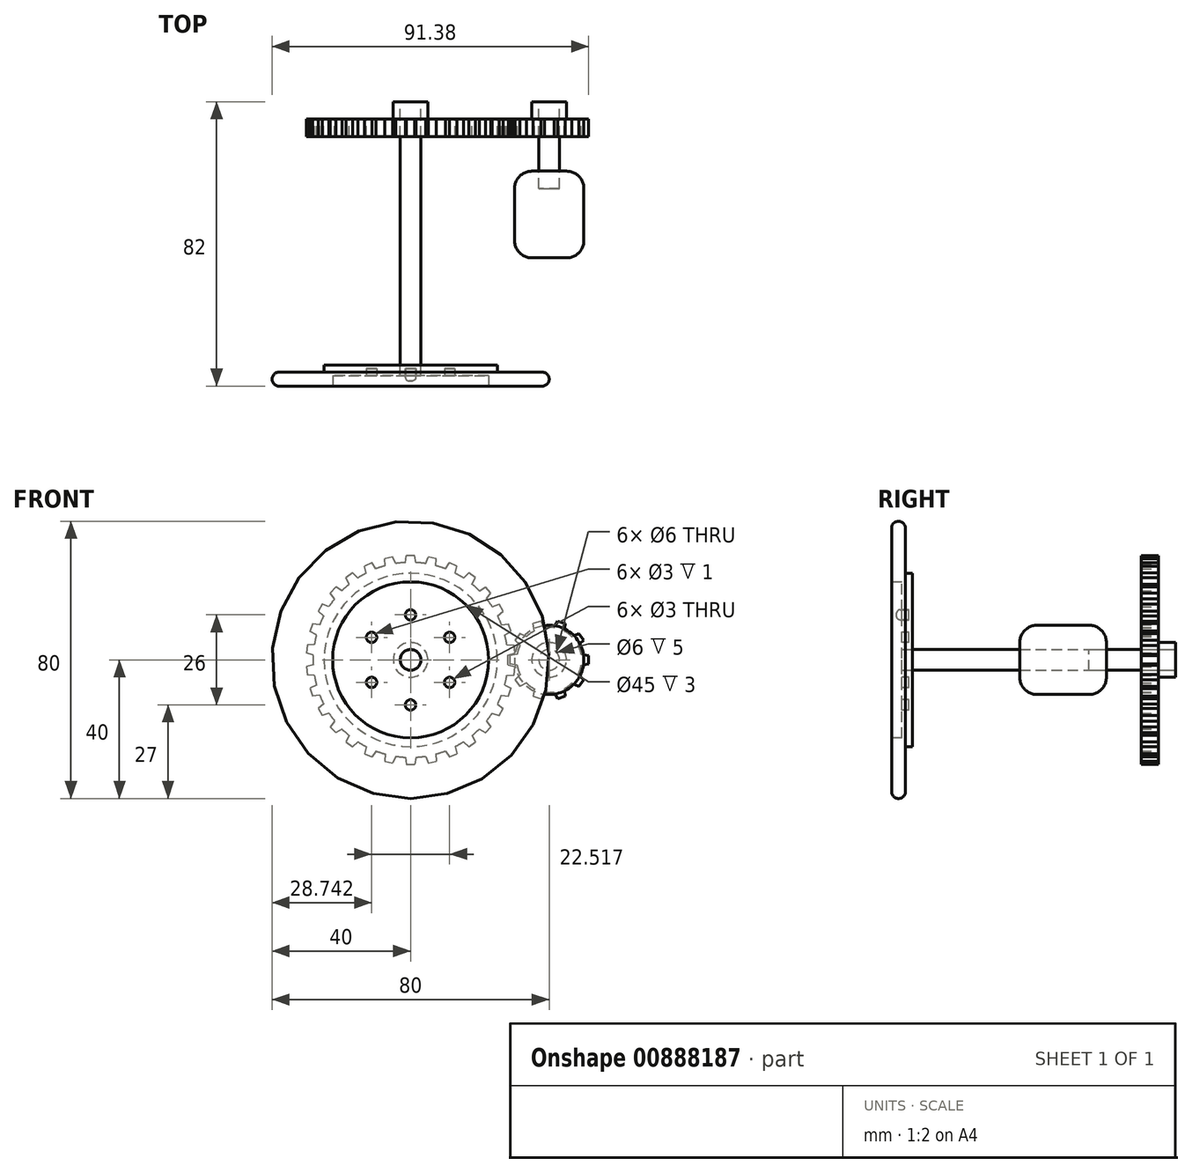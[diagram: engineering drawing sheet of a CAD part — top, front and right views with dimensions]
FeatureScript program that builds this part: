
annotation { "Feature Type Name" : "Feature", "Feature Type Description" : "" }
export const myFeature = defineFeature(function(context is Context, id is Id, definition is map)
    precondition{}
    {
        {
            var Q0;
            Q0=qCreatedBy(makeId("Front.planeOp"),FACE);
            var sketch = newSketch(context, id + "F0", { "sketchPlane" : qUnion([Q0])});
            skCircle(sketch, "E0", {"center": v(0, 0) * mm, "radius": 5 * mm});
            skCircle(sketch, "E1", {"center": v(0, 0) * mm, "radius": 3 * mm});
            skCircle(sketch, "E2", {"center": v(40, 0) * mm, "radius": 5 * mm});
            skCircle(sketch, "E3", {"center": v(40, 0) * mm, "radius": 3 * mm});
            skSolve(sketch);
        }
        {
            var Q0;
            Q0=makeQuery(id+"F0.imprint","IMPRINT",FACE,{"disambiguationData":[TD([[makeQuery(id+"F0.imprint","IMPRINT",EDGE,{"derivedFrom":sQuery(id+"F0.wireOp",EDGE,"E1")}),1.0]])]});
            extrude(context, id + "F1", {"entities" : qUnion([Q0]), "depth" : 80 * mm, "offsetDistance" : 25 * mm});
        }
        {
            var Q0;
            Q0=makeQuery(id+"F0.imprint","IMPRINT",FACE,{"disambiguationData":[TD([[makeQuery(id+"F0.imprint","IMPRINT",EDGE,{"derivedFrom":sQuery(id+"F0.wireOp",EDGE,"E0")}),1.0]])]});
            extrude(context, id + "F2", {"entities" : qUnion([Q0]), "depth" : 5 * mm, "offsetDistance" : 25 * mm});
        }
        {
            var Q0;
            Q0=makeQuery(id+"F0.imprint","IMPRINT",FACE,{"disambiguationData":[TD([[makeQuery(id+"F0.imprint","IMPRINT",EDGE,{"derivedFrom":sQuery(id+"F0.wireOp",EDGE,"E2")}),1.0]])]});
            extrude(context, id + "F3", {"entities" : qUnion([Q0]), "depth" : 5 * mm, "offsetDistance" : 25 * mm});
        }
        {
            var Q0;
            Q0=makeQuery(id+"F0.imprint","IMPRINT",FACE,{"disambiguationData":[TD([[makeQuery(id+"F0.imprint","IMPRINT",EDGE,{"derivedFrom":sQuery(id+"F0.wireOp",EDGE,"E3")}),1.0]])]});
            extrude(context, id + "F4", {"entities" : qUnion([Q0]), "depth" : 25 * mm, "offsetDistance" : 25 * mm});
        }
        {
            var Q0;
            Q0=makeQuery(id+"F2.opExtrude","CAP_FACE",FACE,{"disambiguationData":[OSD([sQuery(id+"F0.wireOp",EDGE,"E0"),sQuery(id+"F0.wireOp",EDGE,"E1")])],"isStart":false});
            var sketch = newSketch(context, id + "F5", { "sketchPlane" : qUnion([Q0])});
            skCircle(sketch, "E4", {"center": v(0, 0) * mm, "radius": 28.12 * mm});
            skLineSegment(sketch, "E5", {"start": v(1.54, 28.08) * mm, "end": v(1.18, 30.12) * mm});
            skLineSegment(sketch, "E6", {"start": v(1.18, 30.12) * mm, "end": v(0, 30.12) * mm});
            skLineSegment(sketch, "E7.MirrorCS", {"start": v(-1.18, 30.13) * mm, "end": v(0, 30.13) * mm});
            skLineSegment(sketch, "E8.MirrorCS", {"start": v(-1.54, 28.08) * mm, "end": v(-1.18, 30.12) * mm});
            skLineSegment(sketch, "E9.1.0", {"start": v(-4.33, 27.79) * mm, "end": v(-5.11, 29.71) * mm});
            skLineSegment(sketch, "E9.1.1", {"start": v(-5.11, 29.71) * mm, "end": v(-6.26, 29.47) * mm});
            skLineSegment(sketch, "E9.1.2", {"start": v(-7.42, 29.22) * mm, "end": v(-6.26, 29.47) * mm});
            skLineSegment(sketch, "E9.1.3", {"start": v(-7.34, 27.15) * mm, "end": v(-7.42, 29.22) * mm});
            skLineSegment(sketch, "E9.2.0", {"start": v(-10.02, 26.28) * mm, "end": v(-11.18, 28) * mm});
            skLineSegment(sketch, "E9.2.1", {"start": v(-11.18, 28) * mm, "end": v(-12.25, 27.52) * mm});
            skLineSegment(sketch, "E9.2.2", {"start": v(-13.33, 27.04) * mm, "end": v(-12.25, 27.52) * mm});
            skLineSegment(sketch, "E9.2.3", {"start": v(-12.83, 25.03) * mm, "end": v(-13.33, 27.04) * mm});
            skLineSegment(sketch, "E10.1.3.0", {"start": v(-15.26, 23.62) * mm, "end": v(-16.75, 25.06) * mm});
            skLineSegment(sketch, "E10.3.3.0", {"start": v(-16.75, 25.06) * mm, "end": v(-17.7, 24.37) * mm});
            skLineSegment(sketch, "E10.6.3.0", {"start": v(-18.66, 23.68) * mm, "end": v(-17.7, 24.37) * mm});
            skLineSegment(sketch, "E10.9.3.0", {"start": v(-17.75, 21.82) * mm, "end": v(-18.66, 23.68) * mm});
            skLineSegment(sketch, "E10.1.4.0", {"start": v(-19.84, 19.93) * mm, "end": v(-21.6, 21.03) * mm});
            skLineSegment(sketch, "E10.3.4.0", {"start": v(-21.6, 21.03) * mm, "end": v(-22.39, 20.16) * mm});
            skLineSegment(sketch, "E10.6.4.0", {"start": v(-23.18, 19.28) * mm, "end": v(-22.39, 20.16) * mm});
            skLineSegment(sketch, "E10.9.4.0", {"start": v(-21.9, 17.65) * mm, "end": v(-23.18, 19.28) * mm});
            skLineSegment(sketch, "E10.1.5.0", {"start": v(-23.55, 15.37) * mm, "end": v(-25.5, 16.08) * mm});
            skLineSegment(sketch, "E10.3.5.0", {"start": v(-25.5, 16.08) * mm, "end": v(-26.09, 15.06) * mm});
            skLineSegment(sketch, "E10.6.5.0", {"start": v(-26.68, 14.04) * mm, "end": v(-26.09, 15.06) * mm});
            skLineSegment(sketch, "E10.9.5.0", {"start": v(-25.09, 12.7) * mm, "end": v(-26.68, 14.04) * mm});
            skLineSegment(sketch, "E10.1.6.0", {"start": v(-26.23, 10.14) * mm, "end": v(-28.29, 10.43) * mm});
            skLineSegment(sketch, "E10.3.6.0", {"start": v(-28.29, 10.43) * mm, "end": v(-28.65, 9.3) * mm});
            skLineSegment(sketch, "E10.6.6.0", {"start": v(-29.01, 8.19) * mm, "end": v(-28.65, 9.3) * mm});
            skLineSegment(sketch, "E10.9.6.0", {"start": v(-27.18, 7.22) * mm, "end": v(-29.01, 8.19) * mm});
            skLineSegment(sketch, "E10.1.7.0", {"start": v(-27.77, 4.47) * mm, "end": v(-29.84, 4.32) * mm});
            skLineSegment(sketch, "E10.3.7.0", {"start": v(-29.84, 4.32) * mm, "end": v(-29.96, 3.15) * mm});
            skLineSegment(sketch, "E10.6.7.0", {"start": v(-30.08, 1.98) * mm, "end": v(-29.96, 3.15) * mm});
            skLineSegment(sketch, "E10.9.7.0", {"start": v(-28.09, 1.4) * mm, "end": v(-30.08, 1.98) * mm});
            skLineSegment(sketch, "E10.1.8.0", {"start": v(-28.09, -1.4) * mm, "end": v(-30.08, -1.98) * mm});
            skLineSegment(sketch, "E10.3.8.0", {"start": v(-30.08, -1.98) * mm, "end": v(-29.96, -3.15) * mm});
            skLineSegment(sketch, "E10.6.8.0", {"start": v(-29.84, -4.32) * mm, "end": v(-29.96, -3.15) * mm});
            skLineSegment(sketch, "E10.9.8.0", {"start": v(-27.77, -4.47) * mm, "end": v(-29.84, -4.32) * mm});
            skLineSegment(sketch, "E10.1.9.0", {"start": v(-27.18, -7.22) * mm, "end": v(-29.01, -8.19) * mm});
            skLineSegment(sketch, "E10.3.9.0", {"start": v(-29.01, -8.19) * mm, "end": v(-28.65, -9.3) * mm});
            skLineSegment(sketch, "E10.6.9.0", {"start": v(-28.29, -10.43) * mm, "end": v(-28.65, -9.3) * mm});
            skLineSegment(sketch, "E10.9.9.0", {"start": v(-26.23, -10.14) * mm, "end": v(-28.29, -10.43) * mm});
            skLineSegment(sketch, "E10.1.10.0", {"start": v(-25.09, -12.7) * mm, "end": v(-26.68, -14.04) * mm});
            skLineSegment(sketch, "E10.3.10.0", {"start": v(-26.68, -14.04) * mm, "end": v(-26.09, -15.06) * mm});
            skLineSegment(sketch, "E10.6.10.0", {"start": v(-25.5, -16.08) * mm, "end": v(-26.09, -15.06) * mm});
            skLineSegment(sketch, "E10.9.10.0", {"start": v(-23.55, -15.37) * mm, "end": v(-25.5, -16.08) * mm});
            skLineSegment(sketch, "E10.1.11.0", {"start": v(-21.9, -17.65) * mm, "end": v(-23.18, -19.28) * mm});
            skLineSegment(sketch, "E10.3.11.0", {"start": v(-23.18, -19.28) * mm, "end": v(-22.39, -20.16) * mm});
            skLineSegment(sketch, "E10.6.11.0", {"start": v(-21.6, -21.03) * mm, "end": v(-22.39, -20.16) * mm});
            skLineSegment(sketch, "E10.9.11.0", {"start": v(-19.84, -19.93) * mm, "end": v(-21.6, -21.03) * mm});
            skLineSegment(sketch, "E10.1.12.0", {"start": v(-17.75, -21.82) * mm, "end": v(-18.66, -23.68) * mm});
            skLineSegment(sketch, "E10.3.12.0", {"start": v(-18.66, -23.68) * mm, "end": v(-17.7, -24.37) * mm});
            skLineSegment(sketch, "E10.6.12.0", {"start": v(-16.75, -25.06) * mm, "end": v(-17.7, -24.37) * mm});
            skLineSegment(sketch, "E10.9.12.0", {"start": v(-15.26, -23.62) * mm, "end": v(-16.75, -25.06) * mm});
            skLineSegment(sketch, "E10.1.13.0", {"start": v(-12.83, -25.03) * mm, "end": v(-13.33, -27.04) * mm});
            skLineSegment(sketch, "E10.3.13.0", {"start": v(-13.33, -27.04) * mm, "end": v(-12.25, -27.52) * mm});
            skLineSegment(sketch, "E10.6.13.0", {"start": v(-11.18, -28) * mm, "end": v(-12.25, -27.52) * mm});
            skLineSegment(sketch, "E10.9.13.0", {"start": v(-10.02, -26.28) * mm, "end": v(-11.18, -28) * mm});
            skLineSegment(sketch, "E10.1.14.0", {"start": v(-7.34, -27.15) * mm, "end": v(-7.42, -29.22) * mm});
            skLineSegment(sketch, "E10.3.14.0", {"start": v(-7.42, -29.22) * mm, "end": v(-6.26, -29.47) * mm});
            skLineSegment(sketch, "E10.6.14.0", {"start": v(-5.11, -29.71) * mm, "end": v(-6.26, -29.47) * mm});
            skLineSegment(sketch, "E10.9.14.0", {"start": v(-4.33, -27.79) * mm, "end": v(-5.11, -29.71) * mm});
            skLineSegment(sketch, "E10.1.15.0", {"start": v(-1.54, -28.08) * mm, "end": v(-1.18, -30.12) * mm});
            skLineSegment(sketch, "E10.3.15.0", {"start": v(-1.18, -30.13) * mm, "end": v(0, -30.13) * mm});
            skLineSegment(sketch, "E10.6.15.0", {"start": v(1.18, -30.13) * mm, "end": v(0, -30.13) * mm});
            skLineSegment(sketch, "E10.9.15.0", {"start": v(1.54, -28.08) * mm, "end": v(1.18, -30.12) * mm});
            skLineSegment(sketch, "E10.1.16.0", {"start": v(4.33, -27.79) * mm, "end": v(5.11, -29.71) * mm});
            skLineSegment(sketch, "E10.3.16.0", {"start": v(5.11, -29.71) * mm, "end": v(6.26, -29.47) * mm});
            skLineSegment(sketch, "E10.6.16.0", {"start": v(7.42, -29.22) * mm, "end": v(6.26, -29.47) * mm});
            skLineSegment(sketch, "E10.9.16.0", {"start": v(7.34, -27.15) * mm, "end": v(7.42, -29.22) * mm});
            skLineSegment(sketch, "E10.1.17.0", {"start": v(10.02, -26.28) * mm, "end": v(11.18, -28) * mm});
            skLineSegment(sketch, "E10.3.17.0", {"start": v(11.18, -28) * mm, "end": v(12.25, -27.52) * mm});
            skLineSegment(sketch, "E10.6.17.0", {"start": v(13.33, -27.04) * mm, "end": v(12.25, -27.52) * mm});
            skLineSegment(sketch, "E10.9.17.0", {"start": v(12.83, -25.03) * mm, "end": v(13.33, -27.04) * mm});
            skLineSegment(sketch, "E10.1.18.0", {"start": v(15.26, -23.62) * mm, "end": v(16.75, -25.06) * mm});
            skLineSegment(sketch, "E10.3.18.0", {"start": v(16.75, -25.06) * mm, "end": v(17.7, -24.37) * mm});
            skLineSegment(sketch, "E10.6.18.0", {"start": v(18.66, -23.68) * mm, "end": v(17.7, -24.37) * mm});
            skLineSegment(sketch, "E10.9.18.0", {"start": v(17.75, -21.82) * mm, "end": v(18.66, -23.68) * mm});
            skLineSegment(sketch, "E10.1.19.0", {"start": v(19.84, -19.93) * mm, "end": v(21.6, -21.03) * mm});
            skLineSegment(sketch, "E10.3.19.0", {"start": v(21.6, -21.03) * mm, "end": v(22.39, -20.16) * mm});
            skLineSegment(sketch, "E10.6.19.0", {"start": v(23.18, -19.28) * mm, "end": v(22.39, -20.16) * mm});
            skLineSegment(sketch, "E10.9.19.0", {"start": v(21.9, -17.65) * mm, "end": v(23.18, -19.28) * mm});
            skLineSegment(sketch, "E10.1.20.0", {"start": v(23.55, -15.37) * mm, "end": v(25.5, -16.08) * mm});
            skLineSegment(sketch, "E10.3.20.0", {"start": v(25.5, -16.08) * mm, "end": v(26.09, -15.06) * mm});
            skLineSegment(sketch, "E10.6.20.0", {"start": v(26.68, -14.04) * mm, "end": v(26.09, -15.06) * mm});
            skLineSegment(sketch, "E10.9.20.0", {"start": v(25.09, -12.7) * mm, "end": v(26.68, -14.04) * mm});
            skLineSegment(sketch, "E10.1.21.0", {"start": v(26.23, -10.14) * mm, "end": v(28.29, -10.43) * mm});
            skLineSegment(sketch, "E10.3.21.0", {"start": v(28.29, -10.43) * mm, "end": v(28.65, -9.3) * mm});
            skLineSegment(sketch, "E10.6.21.0", {"start": v(29.01, -8.19) * mm, "end": v(28.65, -9.3) * mm});
            skLineSegment(sketch, "E10.9.21.0", {"start": v(27.18, -7.22) * mm, "end": v(29.01, -8.19) * mm});
            skLineSegment(sketch, "E10.1.22.0", {"start": v(27.77, -4.47) * mm, "end": v(29.84, -4.32) * mm});
            skLineSegment(sketch, "E10.3.22.0", {"start": v(29.84, -4.32) * mm, "end": v(29.96, -3.15) * mm});
            skLineSegment(sketch, "E10.6.22.0", {"start": v(30.08, -1.98) * mm, "end": v(29.96, -3.15) * mm});
            skLineSegment(sketch, "E10.9.22.0", {"start": v(28.09, -1.4) * mm, "end": v(30.08, -1.98) * mm});
            skLineSegment(sketch, "E10.1.23.0", {"start": v(28.09, 1.4) * mm, "end": v(30.08, 1.98) * mm});
            skLineSegment(sketch, "E10.3.23.0", {"start": v(30.08, 1.98) * mm, "end": v(29.96, 3.15) * mm});
            skLineSegment(sketch, "E10.6.23.0", {"start": v(29.84, 4.32) * mm, "end": v(29.96, 3.15) * mm});
            skLineSegment(sketch, "E10.9.23.0", {"start": v(27.77, 4.47) * mm, "end": v(29.84, 4.32) * mm});
            skLineSegment(sketch, "E10.1.24.0", {"start": v(27.18, 7.22) * mm, "end": v(29.01, 8.19) * mm});
            skLineSegment(sketch, "E10.3.24.0", {"start": v(29.01, 8.19) * mm, "end": v(28.65, 9.3) * mm});
            skLineSegment(sketch, "E10.6.24.0", {"start": v(28.29, 10.43) * mm, "end": v(28.65, 9.3) * mm});
            skLineSegment(sketch, "E10.9.24.0", {"start": v(26.23, 10.14) * mm, "end": v(28.29, 10.43) * mm});
            skLineSegment(sketch, "E10.1.25.0", {"start": v(25.09, 12.7) * mm, "end": v(26.68, 14.04) * mm});
            skLineSegment(sketch, "E10.3.25.0", {"start": v(26.68, 14.04) * mm, "end": v(26.09, 15.06) * mm});
            skLineSegment(sketch, "E10.6.25.0", {"start": v(25.5, 16.08) * mm, "end": v(26.09, 15.06) * mm});
            skLineSegment(sketch, "E10.9.25.0", {"start": v(23.55, 15.37) * mm, "end": v(25.5, 16.08) * mm});
            skLineSegment(sketch, "E10.1.26.0", {"start": v(21.9, 17.65) * mm, "end": v(23.18, 19.28) * mm});
            skLineSegment(sketch, "E10.3.26.0", {"start": v(23.18, 19.28) * mm, "end": v(22.39, 20.16) * mm});
            skLineSegment(sketch, "E10.6.26.0", {"start": v(21.6, 21.03) * mm, "end": v(22.39, 20.16) * mm});
            skLineSegment(sketch, "E10.9.26.0", {"start": v(19.84, 19.93) * mm, "end": v(21.6, 21.03) * mm});
            skLineSegment(sketch, "E10.1.27.0", {"start": v(17.75, 21.82) * mm, "end": v(18.66, 23.68) * mm});
            skLineSegment(sketch, "E10.3.27.0", {"start": v(18.66, 23.68) * mm, "end": v(17.7, 24.37) * mm});
            skLineSegment(sketch, "E10.6.27.0", {"start": v(16.75, 25.06) * mm, "end": v(17.7, 24.37) * mm});
            skLineSegment(sketch, "E10.9.27.0", {"start": v(15.26, 23.62) * mm, "end": v(16.75, 25.06) * mm});
            skLineSegment(sketch, "E10.1.28.0", {"start": v(12.83, 25.03) * mm, "end": v(13.33, 27.04) * mm});
            skLineSegment(sketch, "E10.3.28.0", {"start": v(13.33, 27.04) * mm, "end": v(12.25, 27.52) * mm});
            skLineSegment(sketch, "E10.6.28.0", {"start": v(11.18, 28) * mm, "end": v(12.25, 27.52) * mm});
            skLineSegment(sketch, "E10.9.28.0", {"start": v(10.02, 26.28) * mm, "end": v(11.18, 28) * mm});
            skLineSegment(sketch, "E10.1.29.0", {"start": v(7.34, 27.15) * mm, "end": v(7.42, 29.22) * mm});
            skLineSegment(sketch, "E10.3.29.0", {"start": v(7.42, 29.22) * mm, "end": v(6.26, 29.47) * mm});
            skLineSegment(sketch, "E10.6.29.0", {"start": v(5.11, 29.71) * mm, "end": v(6.26, 29.47) * mm});
            skLineSegment(sketch, "E10.9.29.0", {"start": v(4.33, 27.79) * mm, "end": v(5.11, 29.71) * mm});
            skSolve(sketch);
        }
        {
            var Q0;
            Q0 = qSketchRegion(id + "F5", true);
            extrude(context, id + "F6", {"entities" : qUnion([Q0]), "depth" : 5 * mm, "offsetDistance" : 25 * mm});
        }
        {
            var Q0;
            Q0=makeQuery(id+"F3.opExtrude","CAP_FACE",FACE,{"disambiguationData":[OSD([sQuery(id+"F0.wireOp",EDGE,"E2"),sQuery(id+"F0.wireOp",EDGE,"E3")])],"isStart":false});
            var sketch = newSketch(context, id + "F7", { "sketchPlane" : qUnion([Q0])});
            skCircle(sketch, "E11", {"center": v(40, 0) * mm, "radius": 9.38 * mm});
            skLineSegment(sketch, "E12", {"start": v(30.75, 1.55) * mm, "end": v(28.62, 1.18) * mm});
            skLineSegment(sketch, "E13", {"start": v(28.62, 1.18) * mm, "end": v(28.62, 0) * mm});
            skLineSegment(sketch, "E14.MirrorCS", {"start": v(28.62, -1.18) * mm, "end": v(28.62, 0) * mm});
            skLineSegment(sketch, "E15.MirrorCS", {"start": v(30.75, -1.55) * mm, "end": v(28.62, -1.18) * mm});
            skLineSegment(sketch, "E16.1.0", {"start": v(31.6, -4.18) * mm, "end": v(30.1, -5.73) * mm});
            skLineSegment(sketch, "E16.1.1", {"start": v(30.1, -5.73) * mm, "end": v(30.8, -6.69) * mm});
            skLineSegment(sketch, "E16.1.2", {"start": v(31.49, -7.64) * mm, "end": v(30.8, -6.69) * mm});
            skLineSegment(sketch, "E16.1.3", {"start": v(33.43, -6.7) * mm, "end": v(31.49, -7.64) * mm});
            skLineSegment(sketch, "E16.2.0", {"start": v(35.67, -8.31) * mm, "end": v(35.36, -10.45) * mm});
            skLineSegment(sketch, "E16.2.1", {"start": v(35.36, -10.45) * mm, "end": v(36.48, -10.82) * mm});
            skLineSegment(sketch, "E16.2.2", {"start": v(37.6, -11.18) * mm, "end": v(36.48, -10.82) * mm});
            skLineSegment(sketch, "E16.2.3", {"start": v(38.62, -9.27) * mm, "end": v(37.6, -11.18) * mm});
            skLineSegment(sketch, "E17.2.3.0", {"start": v(41.38, -9.27) * mm, "end": v(42.4, -11.18) * mm});
            skLineSegment(sketch, "E17.3.3.0", {"start": v(42.4, -11.18) * mm, "end": v(43.52, -10.82) * mm});
            skLineSegment(sketch, "E17.6.3.0", {"start": v(44.64, -10.45) * mm, "end": v(43.52, -10.82) * mm});
            skLineSegment(sketch, "E17.9.3.0", {"start": v(44.33, -8.31) * mm, "end": v(44.64, -10.45) * mm});
            skLineSegment(sketch, "E17.2.4.0", {"start": v(46.57, -6.7) * mm, "end": v(48.51, -7.64) * mm});
            skLineSegment(sketch, "E17.3.4.0", {"start": v(48.51, -7.64) * mm, "end": v(49.2, -6.69) * mm});
            skLineSegment(sketch, "E17.6.4.0", {"start": v(49.9, -5.73) * mm, "end": v(49.2, -6.69) * mm});
            skLineSegment(sketch, "E17.9.4.0", {"start": v(48.4, -4.18) * mm, "end": v(49.9, -5.73) * mm});
            skLineSegment(sketch, "E17.2.5.0", {"start": v(49.25, -1.55) * mm, "end": v(51.38, -1.18) * mm});
            skLineSegment(sketch, "E17.3.5.0", {"start": v(51.38, -1.18) * mm, "end": v(51.38, 0) * mm});
            skLineSegment(sketch, "E17.6.5.0", {"start": v(51.38, 1.18) * mm, "end": v(51.38, 0) * mm});
            skLineSegment(sketch, "E17.9.5.0", {"start": v(49.25, 1.55) * mm, "end": v(51.38, 1.18) * mm});
            skLineSegment(sketch, "E17.2.6.0", {"start": v(48.4, 4.18) * mm, "end": v(49.9, 5.73) * mm});
            skLineSegment(sketch, "E17.3.6.0", {"start": v(49.9, 5.73) * mm, "end": v(49.2, 6.69) * mm});
            skLineSegment(sketch, "E17.6.6.0", {"start": v(48.51, 7.64) * mm, "end": v(49.2, 6.69) * mm});
            skLineSegment(sketch, "E17.9.6.0", {"start": v(46.57, 6.7) * mm, "end": v(48.51, 7.64) * mm});
            skLineSegment(sketch, "E17.2.7.0", {"start": v(44.33, 8.31) * mm, "end": v(44.64, 10.45) * mm});
            skLineSegment(sketch, "E17.3.7.0", {"start": v(44.64, 10.45) * mm, "end": v(43.52, 10.82) * mm});
            skLineSegment(sketch, "E17.6.7.0", {"start": v(42.4, 11.18) * mm, "end": v(43.52, 10.82) * mm});
            skLineSegment(sketch, "E17.9.7.0", {"start": v(41.38, 9.27) * mm, "end": v(42.4, 11.18) * mm});
            skLineSegment(sketch, "E17.2.8.0", {"start": v(38.62, 9.27) * mm, "end": v(37.6, 11.18) * mm});
            skLineSegment(sketch, "E17.3.8.0", {"start": v(37.6, 11.18) * mm, "end": v(36.48, 10.82) * mm});
            skLineSegment(sketch, "E17.6.8.0", {"start": v(35.36, 10.45) * mm, "end": v(36.48, 10.82) * mm});
            skLineSegment(sketch, "E17.9.8.0", {"start": v(35.67, 8.31) * mm, "end": v(35.36, 10.45) * mm});
            skLineSegment(sketch, "E17.2.9.0", {"start": v(33.43, 6.7) * mm, "end": v(31.49, 7.64) * mm});
            skLineSegment(sketch, "E17.3.9.0", {"start": v(31.49, 7.64) * mm, "end": v(30.8, 6.69) * mm});
            skLineSegment(sketch, "E17.6.9.0", {"start": v(30.1, 5.73) * mm, "end": v(30.8, 6.69) * mm});
            skLineSegment(sketch, "E17.9.9.0", {"start": v(31.6, 4.18) * mm, "end": v(30.1, 5.73) * mm});
            skSolve(sketch);
        }
        {
            var Q0;
            Q0 = qSketchRegion(id + "F7", true);
            extrude(context, id + "F8", {"entities" : qUnion([Q0]), "depth" : 5 * mm, "offsetDistance" : 25 * mm});
        }
        {
            var Q0;
            Q0=makeQuery(id+"F1.opExtrude","CAP_FACE",FACE,{"disambiguationData":[OSD([sQuery(id+"F0.wireOp",EDGE,"E1")])],"isStart":false});
            var sketch = newSketch(context, id + "F9", { "sketchPlane" : qUnion([Q0])});
            skCircle(sketch, "E18", {"center": v(0, 0) * mm, "radius": 40 * mm});
            skSolve(sketch);
        }
        {
            var Q0;
            Q0 = qSketchRegion(id + "F9", true);
            extrude(context, id + "F10", {"entities" : qUnion([Q0]), "endBound" : BoundingType.SYMMETRIC, "depth" : 4 * mm, "offsetDistance" : 25 * mm});
        }
        {
            var Q0;
            Q0=makeQuery(id+"F1.opExtrude","SWEPT_BODY",BODY,{"disambiguationData":[OSD([sQuery(id+"F0.wireOp",EDGE,"E1")])]});
            var Q1;
            Q1=makeQuery(id+"F10.opExtrude","SWEPT_BODY",BODY,{"disambiguationData":[OSD([sQuery(id+"F9.wireOp",EDGE,"E18")])]});
            booleanBodies(context, id + "F11", {"operationType" : BooleanOperationType.SUBTRACTION, "tools" : qUnion([Q0]), "targets" : qUnion([Q1]), "keepTools" : true});
        }
        {
            var Q0;
            Q0=makeQuery(id+"F4.opExtrude","CAP_FACE",FACE,{"disambiguationData":[OSD([sQuery(id+"F0.wireOp",EDGE,"E3")])],"isStart":false});
            var sketch = newSketch(context, id + "F12", { "sketchPlane" : qUnion([Q0])});
            skCircle(sketch, "E19", {"center": v(40, 0) * mm, "radius": 10 * mm});
            skSolve(sketch);
        }
        {
            var Q0;
            Q0 = qSketchRegion(id + "F12", true);
            extrude(context, id + "F13", {"entities" : qUnion([Q0]), "depth" : 25 * mm, "offsetDistance" : 25 * mm});
        }
        {
            var Q0;
            Q0=makeQuery(id+"F13.opExtrude","SWEPT_BODY",BODY,{"disambiguationData":[OSD([sQuery(id+"F12.wireOp",EDGE,"E19")])]});
            transform(context, id + "F14", {"entities" : qUnion([Q0]), "transformType" : TransformType.TRANSLATION_3D, "dx" : 0 * mm, "dy" : 5 * mm, "dz" : 0 * mm, "makeCopy" : false});
        }
        {
            var Q0;
            Q0=makeQuery(id+"F4.opExtrude","SWEPT_BODY",BODY,{"disambiguationData":[OSD([sQuery(id+"F0.wireOp",EDGE,"E3")])]});
            var Q1;
            Q1=makeQuery(id+"F13.opExtrude","SWEPT_BODY",BODY,{"disambiguationData":[OSD([sQuery(id+"F12.wireOp",EDGE,"E19")])]});
            booleanBodies(context, id + "F15", {"operationType" : BooleanOperationType.SUBTRACTION, "tools" : qUnion([Q0]), "targets" : qUnion([Q1]), "keepTools" : true});
        }
        {
            var Q0;
            Q0=makeQuery(id+"F10.opExtrude","CAP_FACE",FACE,{"disambiguationData":[OSD([sQuery(id+"F9.wireOp",EDGE,"E18")])],"isStart":true});
            var sketch = newSketch(context, id + "F16", { "sketchPlane" : qUnion([Q0])});
            skCircle(sketch, "E20", {"center": v(0, 0) * mm, "radius": 25 * mm});
            skSolve(sketch);
        }
        {
            var Q0;
            Q0 = qSketchRegion(id + "F16", true);
            extrude(context, id + "F17", {"entities" : qUnion([Q0]), "depth" : 2 * mm, "offsetDistance" : 25 * mm});
        }
        {
            var Q0;
            Q0=makeQuery(id+"F1.opExtrude","SWEPT_BODY",BODY,{"disambiguationData":[OSD([sQuery(id+"F0.wireOp",EDGE,"E1")])]});
            var Q1;
            Q1=makeQuery(id+"F17.opExtrude","SWEPT_BODY",BODY,{"disambiguationData":[OSD([sQuery(id+"F16.wireOp",EDGE,"E20")])]});
            booleanBodies(context, id + "F18", {"operationType" : BooleanOperationType.SUBTRACTION, "tools" : qUnion([Q0]), "targets" : qUnion([Q1]), "keepTools" : true});
        }
        {
            var Q0;
            Q0=makeQuery(id+"F10.opExtrude","CAP_FACE",FACE,{"disambiguationData":[OSD([sQuery(id+"F9.wireOp",EDGE,"E18")])],"isStart":false});
            var sketch = newSketch(context, id + "F19", { "sketchPlane" : qUnion([Q0])});
            skCircle(sketch, "E21", {"center": v(0, 0) * mm, "radius": 22.5 * mm});
            skSolve(sketch);
        }
        {
            var Q0;
            Q0 = qSketchRegion(id + "F19", true);
            extrude(context, id + "F20", {"entities" : qUnion([Q0]), "operationType" : NewBodyOperationType.REMOVE, "oppositeDirection" : true, "depth" : 3 * mm, "offsetDistance" : 25 * mm});
        }
        {
            var Q0;
            Q0=makeQuery(id+"F20.boolean.opBoolean","COPY",FACE,{"derivedFrom":makeQuery(id+"F20.opExtrude","CAP_FACE",FACE,{"disambiguationData":[OSD([sQuery(id+"F19.wireOp",EDGE,"E21")])],"isStart":false})});
            var sketch = newSketch(context, id + "F21", { "sketchPlane" : qUnion([Q0])});
            skCircle(sketch, "E22", {"center": v(0, 13) * mm, "radius": 1.5 * mm});
            skCircle(sketch, "E23.1.0", {"center": v(-11.26, 6.5) * mm, "radius": 1.5 * mm});
            skCircle(sketch, "E23.2.0", {"center": v(-11.26, -6.5) * mm, "radius": 1.5 * mm});
            skPoint(sketch, "E23.center", {"position": v(0, 0) * mm});
            skCircle(sketch, "E24.1.3.0", {"center": v(0, -13) * mm, "radius": 1.5 * mm});
            skCircle(sketch, "E24.1.4.0", {"center": v(11.26, -6.5) * mm, "radius": 1.5 * mm});
            skCircle(sketch, "E24.1.5.0", {"center": v(11.26, 6.5) * mm, "radius": 1.5 * mm});
            skSolve(sketch);
        }
        {
            var Q0;
            Q0 = qSketchRegion(id + "F21", true);
            extrude(context, id + "F22", {"entities" : qUnion([Q0]), "operationType" : NewBodyOperationType.REMOVE, "oppositeDirection" : true, "depth" : 2 * mm, "offsetDistance" : 25 * mm});
        }
        {
            var Q0;
            Q0=makeQuery(id+"F22.boolean.opBoolean","COPY",FACE,{"derivedFrom":makeQuery(id+"F22.opExtrude","CAP_FACE",FACE,{"disambiguationData":[OSD([sQuery(id+"F21.wireOp",EDGE,"E22")])],"isStart":false})});
            extrude(context, id + "F23", {"entities" : qUnion([Q0]), "depth" : 3.5 * mm, "offsetDistance" : 25 * mm});
        }
        {
            var Q0;
            Q0=makeQuery(id+"F23.opExtrude","CAP_EDGE",EDGE,{"disambiguationData":[OSD([sQuery(id+"F21.wireOp",EDGE,"E22")])],"isStart":false});
            fillet(context, id + "F24", {"entities" : qUnion([Q0]), "radius" : 1 * mm, "tangentPropagation" : true, "allowEdgeOverflow" : false});
        }
        {
            var Q0;
            Q0=makeQuery(id+"F10.opExtrude","CAP_EDGE",EDGE,{"disambiguationData":[OSD([sQuery(id+"F9.wireOp",EDGE,"E18")])],"isStart":false});
            var Q1;
            Q1=makeQuery(id+"F10.opExtrude","CAP_EDGE",EDGE,{"disambiguationData":[OSD([sQuery(id+"F9.wireOp",EDGE,"E18")])],"isStart":true});
            fillet(context, id + "F25", {"entities" : qUnion([Q0, Q1]), "radius" : 2 * mm, "tangentPropagation" : true, "allowEdgeOverflow" : false});
        }
        {
            var Q0;
            Q0=makeQuery(id+"F13.opExtrude","CAP_EDGE",EDGE,{"disambiguationData":[OSD([sQuery(id+"F12.wireOp",EDGE,"E19")])],"isStart":false});
            var Q1;
            Q1=makeQuery(id+"F13.opExtrude","CAP_EDGE",EDGE,{"disambiguationData":[OSD([sQuery(id+"F12.wireOp",EDGE,"E19")])],"isStart":true});
            fillet(context, id + "F26", {"entities" : qUnion([Q0, Q1]), "radius" : 5 * mm, "tangentPropagation" : true, "allowEdgeOverflow" : false});
        }
        {
            var Q0;
            Q0=makeQuery(id+"F1.opExtrude","SWEPT_BODY",BODY,{"disambiguationData":[OSD([sQuery(id+"F0.wireOp",EDGE,"E1")])]});
            var Q1;
            Q1=makeQuery(id+"F6.opExtrude","SWEPT_BODY",BODY,{"disambiguationData":[OSD([sQuery(id+"F5.wireOp",EDGE,"E4"),sQuery(id+"F5.wireOp",EDGE,"E5"),sQuery(id+"F5.wireOp",EDGE,"E6"),sQuery(id+"F5.wireOp",EDGE,"E7.MirrorCS"),sQuery(id+"F5.wireOp",EDGE,"E8.MirrorCS"),sQuery(id+"F5.wireOp",EDGE,"E9.1.0"),sQuery(id+"F5.wireOp",EDGE,"E9.1.1"),sQuery(id+"F5.wireOp",EDGE,"E9.1.2"),sQuery(id+"F5.wireOp",EDGE,"E9.1.3"),sQuery(id+"F5.wireOp",EDGE,"E9.2.0"),sQuery(id+"F5.wireOp",EDGE,"E9.2.1"),sQuery(id+"F5.wireOp",EDGE,"E9.2.2"),sQuery(id+"F5.wireOp",EDGE,"E9.2.3"),sQuery(id+"F5.wireOp",EDGE,"E10.1.3.0"),sQuery(id+"F5.wireOp",EDGE,"E10.3.3.0"),sQuery(id+"F5.wireOp",EDGE,"E10.6.3.0"),sQuery(id+"F5.wireOp",EDGE,"E10.9.3.0"),sQuery(id+"F5.wireOp",EDGE,"E10.1.4.0"),sQuery(id+"F5.wireOp",EDGE,"E10.3.4.0"),sQuery(id+"F5.wireOp",EDGE,"E10.6.4.0"),sQuery(id+"F5.wireOp",EDGE,"E10.9.4.0"),sQuery(id+"F5.wireOp",EDGE,"E10.1.5.0"),sQuery(id+"F5.wireOp",EDGE,"E10.3.5.0"),sQuery(id+"F5.wireOp",EDGE,"E10.6.5.0"),sQuery(id+"F5.wireOp",EDGE,"E10.9.5.0"),sQuery(id+"F5.wireOp",EDGE,"E10.1.6.0"),sQuery(id+"F5.wireOp",EDGE,"E10.3.6.0"),sQuery(id+"F5.wireOp",EDGE,"E10.6.6.0"),sQuery(id+"F5.wireOp",EDGE,"E10.9.6.0"),sQuery(id+"F5.wireOp",EDGE,"E10.1.7.0"),sQuery(id+"F5.wireOp",EDGE,"E10.3.7.0"),sQuery(id+"F5.wireOp",EDGE,"E10.6.7.0"),sQuery(id+"F5.wireOp",EDGE,"E10.9.7.0"),sQuery(id+"F5.wireOp",EDGE,"E10.1.8.0"),sQuery(id+"F5.wireOp",EDGE,"E10.3.8.0"),sQuery(id+"F5.wireOp",EDGE,"E10.6.8.0"),sQuery(id+"F5.wireOp",EDGE,"E10.9.8.0"),sQuery(id+"F5.wireOp",EDGE,"E10.1.9.0"),sQuery(id+"F5.wireOp",EDGE,"E10.3.9.0"),sQuery(id+"F5.wireOp",EDGE,"E10.6.9.0"),sQuery(id+"F5.wireOp",EDGE,"E10.9.9.0"),sQuery(id+"F5.wireOp",EDGE,"E10.1.10.0"),sQuery(id+"F5.wireOp",EDGE,"E10.3.10.0"),sQuery(id+"F5.wireOp",EDGE,"E10.6.10.0"),sQuery(id+"F5.wireOp",EDGE,"E10.9.10.0"),sQuery(id+"F5.wireOp",EDGE,"E10.1.11.0"),sQuery(id+"F5.wireOp",EDGE,"E10.3.11.0"),sQuery(id+"F5.wireOp",EDGE,"E10.6.11.0"),sQuery(id+"F5.wireOp",EDGE,"E10.9.11.0"),sQuery(id+"F5.wireOp",EDGE,"E10.1.12.0"),sQuery(id+"F5.wireOp",EDGE,"E10.3.12.0"),sQuery(id+"F5.wireOp",EDGE,"E10.6.12.0"),sQuery(id+"F5.wireOp",EDGE,"E10.9.12.0"),sQuery(id+"F5.wireOp",EDGE,"E10.1.13.0"),sQuery(id+"F5.wireOp",EDGE,"E10.3.13.0"),sQuery(id+"F5.wireOp",EDGE,"E10.6.13.0"),sQuery(id+"F5.wireOp",EDGE,"E10.9.13.0"),sQuery(id+"F5.wireOp",EDGE,"E10.1.14.0"),sQuery(id+"F5.wireOp",EDGE,"E10.3.14.0"),sQuery(id+"F5.wireOp",EDGE,"E10.6.14.0"),sQuery(id+"F5.wireOp",EDGE,"E10.9.14.0"),sQuery(id+"F5.wireOp",EDGE,"E10.1.15.0"),sQuery(id+"F5.wireOp",EDGE,"E10.3.15.0"),sQuery(id+"F5.wireOp",EDGE,"E10.6.15.0"),sQuery(id+"F5.wireOp",EDGE,"E10.9.15.0"),sQuery(id+"F5.wireOp",EDGE,"E10.1.16.0"),sQuery(id+"F5.wireOp",EDGE,"E10.3.16.0"),sQuery(id+"F5.wireOp",EDGE,"E10.6.16.0"),sQuery(id+"F5.wireOp",EDGE,"E10.9.16.0"),sQuery(id+"F5.wireOp",EDGE,"E10.1.17.0"),sQuery(id+"F5.wireOp",EDGE,"E10.3.17.0"),sQuery(id+"F5.wireOp",EDGE,"E10.6.17.0"),sQuery(id+"F5.wireOp",EDGE,"E10.9.17.0"),sQuery(id+"F5.wireOp",EDGE,"E10.1.18.0"),sQuery(id+"F5.wireOp",EDGE,"E10.3.18.0"),sQuery(id+"F5.wireOp",EDGE,"E10.6.18.0"),sQuery(id+"F5.wireOp",EDGE,"E10.9.18.0"),sQuery(id+"F5.wireOp",EDGE,"E10.1.19.0"),sQuery(id+"F5.wireOp",EDGE,"E10.3.19.0"),sQuery(id+"F5.wireOp",EDGE,"E10.6.19.0"),sQuery(id+"F5.wireOp",EDGE,"E10.9.19.0"),sQuery(id+"F5.wireOp",EDGE,"E10.1.20.0"),sQuery(id+"F5.wireOp",EDGE,"E10.3.20.0"),sQuery(id+"F5.wireOp",EDGE,"E10.6.20.0"),sQuery(id+"F5.wireOp",EDGE,"E10.9.20.0"),sQuery(id+"F5.wireOp",EDGE,"E10.1.21.0"),sQuery(id+"F5.wireOp",EDGE,"E10.3.21.0"),sQuery(id+"F5.wireOp",EDGE,"E10.6.21.0"),sQuery(id+"F5.wireOp",EDGE,"E10.9.21.0"),sQuery(id+"F5.wireOp",EDGE,"E10.1.22.0"),sQuery(id+"F5.wireOp",EDGE,"E10.3.22.0"),sQuery(id+"F5.wireOp",EDGE,"E10.6.22.0"),sQuery(id+"F5.wireOp",EDGE,"E10.9.22.0"),sQuery(id+"F5.wireOp",EDGE,"E10.1.23.0"),sQuery(id+"F5.wireOp",EDGE,"E10.3.23.0"),sQuery(id+"F5.wireOp",EDGE,"E10.6.23.0"),sQuery(id+"F5.wireOp",EDGE,"E10.9.23.0"),sQuery(id+"F5.wireOp",EDGE,"E10.1.24.0"),sQuery(id+"F5.wireOp",EDGE,"E10.3.24.0"),sQuery(id+"F5.wireOp",EDGE,"E10.6.24.0"),sQuery(id+"F5.wireOp",EDGE,"E10.9.24.0"),sQuery(id+"F5.wireOp",EDGE,"E10.1.25.0"),sQuery(id+"F5.wireOp",EDGE,"E10.3.25.0"),sQuery(id+"F5.wireOp",EDGE,"E10.6.25.0"),sQuery(id+"F5.wireOp",EDGE,"E10.9.25.0"),sQuery(id+"F5.wireOp",EDGE,"E10.1.26.0"),sQuery(id+"F5.wireOp",EDGE,"E10.3.26.0"),sQuery(id+"F5.wireOp",EDGE,"E10.6.26.0"),sQuery(id+"F5.wireOp",EDGE,"E10.9.26.0"),sQuery(id+"F5.wireOp",EDGE,"E10.1.27.0"),sQuery(id+"F5.wireOp",EDGE,"E10.3.27.0"),sQuery(id+"F5.wireOp",EDGE,"E10.6.27.0"),sQuery(id+"F5.wireOp",EDGE,"E10.9.27.0"),sQuery(id+"F5.wireOp",EDGE,"E10.1.28.0"),sQuery(id+"F5.wireOp",EDGE,"E10.3.28.0"),sQuery(id+"F5.wireOp",EDGE,"E10.6.28.0"),sQuery(id+"F5.wireOp",EDGE,"E10.9.28.0"),sQuery(id+"F5.wireOp",EDGE,"E10.1.29.0"),sQuery(id+"F5.wireOp",EDGE,"E10.3.29.0"),sQuery(id+"F5.wireOp",EDGE,"E10.6.29.0"),sQuery(id+"F5.wireOp",EDGE,"E10.9.29.0")])]});
            booleanBodies(context, id + "F27", {"operationType" : BooleanOperationType.SUBTRACTION, "tools" : qUnion([Q0]), "targets" : qUnion([Q1]), "keepTools" : true});
        }
        {
            var Q0;
            Q0=makeQuery(id+"F4.opExtrude","SWEPT_BODY",BODY,{"disambiguationData":[OSD([sQuery(id+"F0.wireOp",EDGE,"E3")])]});
            var Q1;
            Q1=makeQuery(id+"F8.opExtrude","SWEPT_BODY",BODY,{"disambiguationData":[OSD([sQuery(id+"F7.wireOp",EDGE,"E11"),sQuery(id+"F7.wireOp",EDGE,"E12"),sQuery(id+"F7.wireOp",EDGE,"E13"),sQuery(id+"F7.wireOp",EDGE,"E14.MirrorCS"),sQuery(id+"F7.wireOp",EDGE,"E15.MirrorCS"),sQuery(id+"F7.wireOp",EDGE,"E16.1.0"),sQuery(id+"F7.wireOp",EDGE,"E16.1.1"),sQuery(id+"F7.wireOp",EDGE,"E16.1.2"),sQuery(id+"F7.wireOp",EDGE,"E16.1.3"),sQuery(id+"F7.wireOp",EDGE,"E16.2.0"),sQuery(id+"F7.wireOp",EDGE,"E16.2.1"),sQuery(id+"F7.wireOp",EDGE,"E16.2.2"),sQuery(id+"F7.wireOp",EDGE,"E16.2.3"),sQuery(id+"F7.wireOp",EDGE,"E17.2.3.0"),sQuery(id+"F7.wireOp",EDGE,"E17.3.3.0"),sQuery(id+"F7.wireOp",EDGE,"E17.6.3.0"),sQuery(id+"F7.wireOp",EDGE,"E17.9.3.0"),sQuery(id+"F7.wireOp",EDGE,"E17.2.4.0"),sQuery(id+"F7.wireOp",EDGE,"E17.3.4.0"),sQuery(id+"F7.wireOp",EDGE,"E17.6.4.0"),sQuery(id+"F7.wireOp",EDGE,"E17.9.4.0"),sQuery(id+"F7.wireOp",EDGE,"E17.2.5.0"),sQuery(id+"F7.wireOp",EDGE,"E17.3.5.0"),sQuery(id+"F7.wireOp",EDGE,"E17.6.5.0"),sQuery(id+"F7.wireOp",EDGE,"E17.9.5.0"),sQuery(id+"F7.wireOp",EDGE,"E17.2.6.0"),sQuery(id+"F7.wireOp",EDGE,"E17.3.6.0"),sQuery(id+"F7.wireOp",EDGE,"E17.6.6.0"),sQuery(id+"F7.wireOp",EDGE,"E17.9.6.0"),sQuery(id+"F7.wireOp",EDGE,"E17.2.7.0"),sQuery(id+"F7.wireOp",EDGE,"E17.3.7.0"),sQuery(id+"F7.wireOp",EDGE,"E17.6.7.0"),sQuery(id+"F7.wireOp",EDGE,"E17.9.7.0"),sQuery(id+"F7.wireOp",EDGE,"E17.2.8.0"),sQuery(id+"F7.wireOp",EDGE,"E17.3.8.0"),sQuery(id+"F7.wireOp",EDGE,"E17.6.8.0"),sQuery(id+"F7.wireOp",EDGE,"E17.9.8.0"),sQuery(id+"F7.wireOp",EDGE,"E17.2.9.0"),sQuery(id+"F7.wireOp",EDGE,"E17.3.9.0"),sQuery(id+"F7.wireOp",EDGE,"E17.6.9.0"),sQuery(id+"F7.wireOp",EDGE,"E17.9.9.0")])]});
            booleanBodies(context, id + "F28", {"operationType" : BooleanOperationType.SUBTRACTION, "tools" : qUnion([Q0]), "targets" : qUnion([Q1]), "keepTools" : true});
        }
    });
